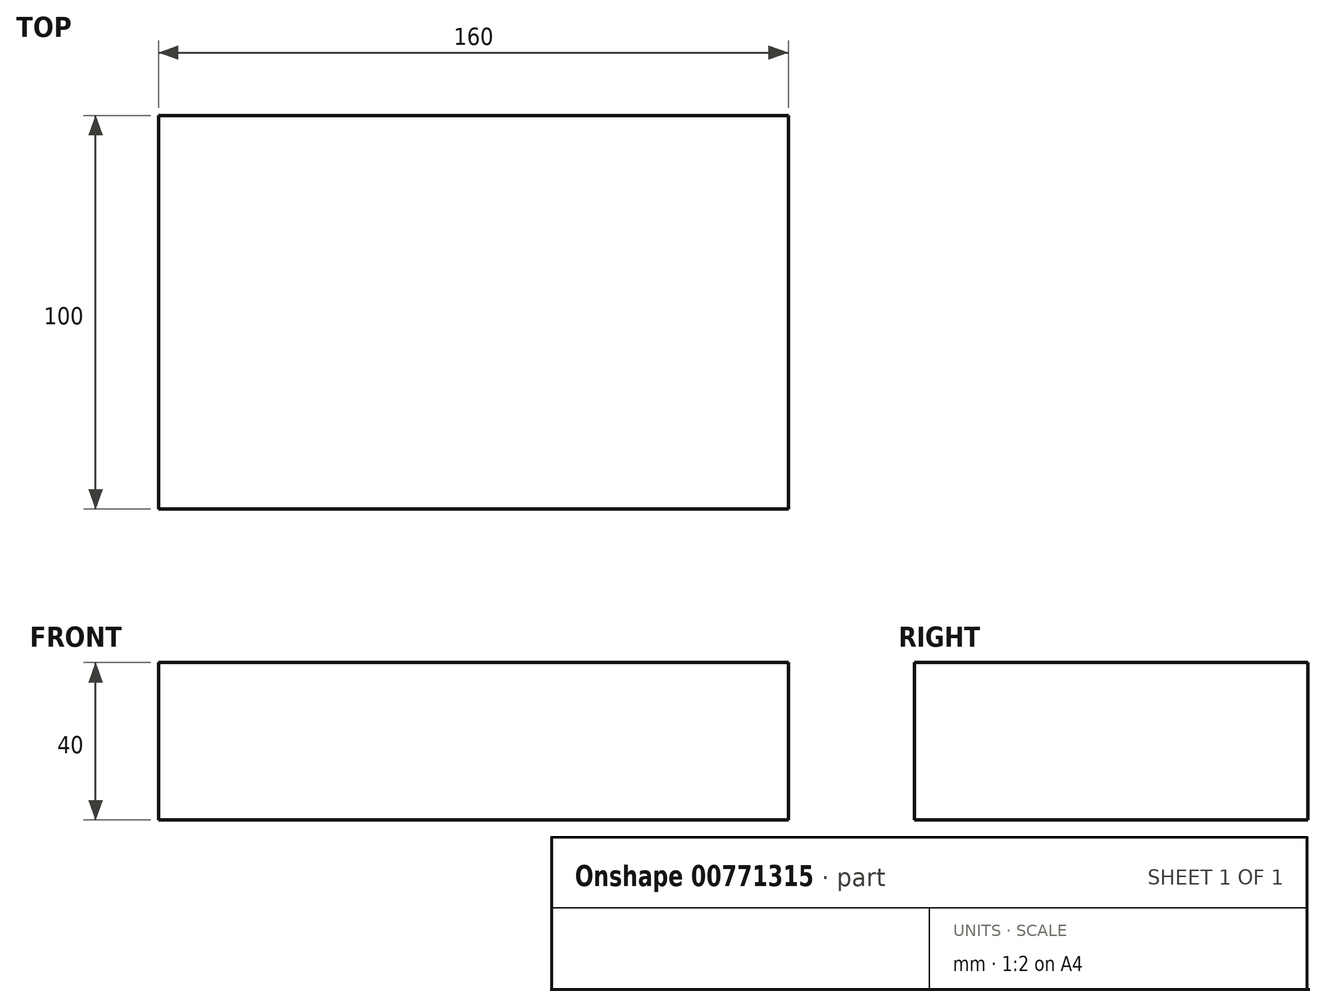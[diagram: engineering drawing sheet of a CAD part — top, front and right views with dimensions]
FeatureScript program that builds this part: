
annotation { "Feature Type Name" : "Feature", "Feature Type Description" : "" }
export const myFeature = defineFeature(function(context is Context, id is Id, definition is map)
    precondition{}
    {
        {
            var Q0;
            Q0=qCreatedBy(makeId("Top.planeOp"),FACE);
            var sketch = newSketch(context, id + "F0", { "sketchPlane" : qUnion([Q0])});
            skLineSegment(sketch, "E0.bottom", {"start": v(0, 0) * mm, "end": v(160, 0) * mm});
            skLineSegment(sketch, "E0.top", {"start": v(0, -100) * mm, "end": v(160, -100) * mm});
            skLineSegment(sketch, "E0.left", {"start": v(0, 0) * mm, "end": v(0, -100) * mm});
            skLineSegment(sketch, "E0.right", {"start": v(160, 0) * mm, "end": v(160, -100) * mm});
            skSolve(sketch);
        }
        {
            var Q0;
            Q0=qSketchRegion(id+"F0",true);
            extrude(context, id + "F1", {"entities" : qUnion([Q0]), "depth" : 40 * mm, "offsetDistance" : 25 * mm});
        }
    });
